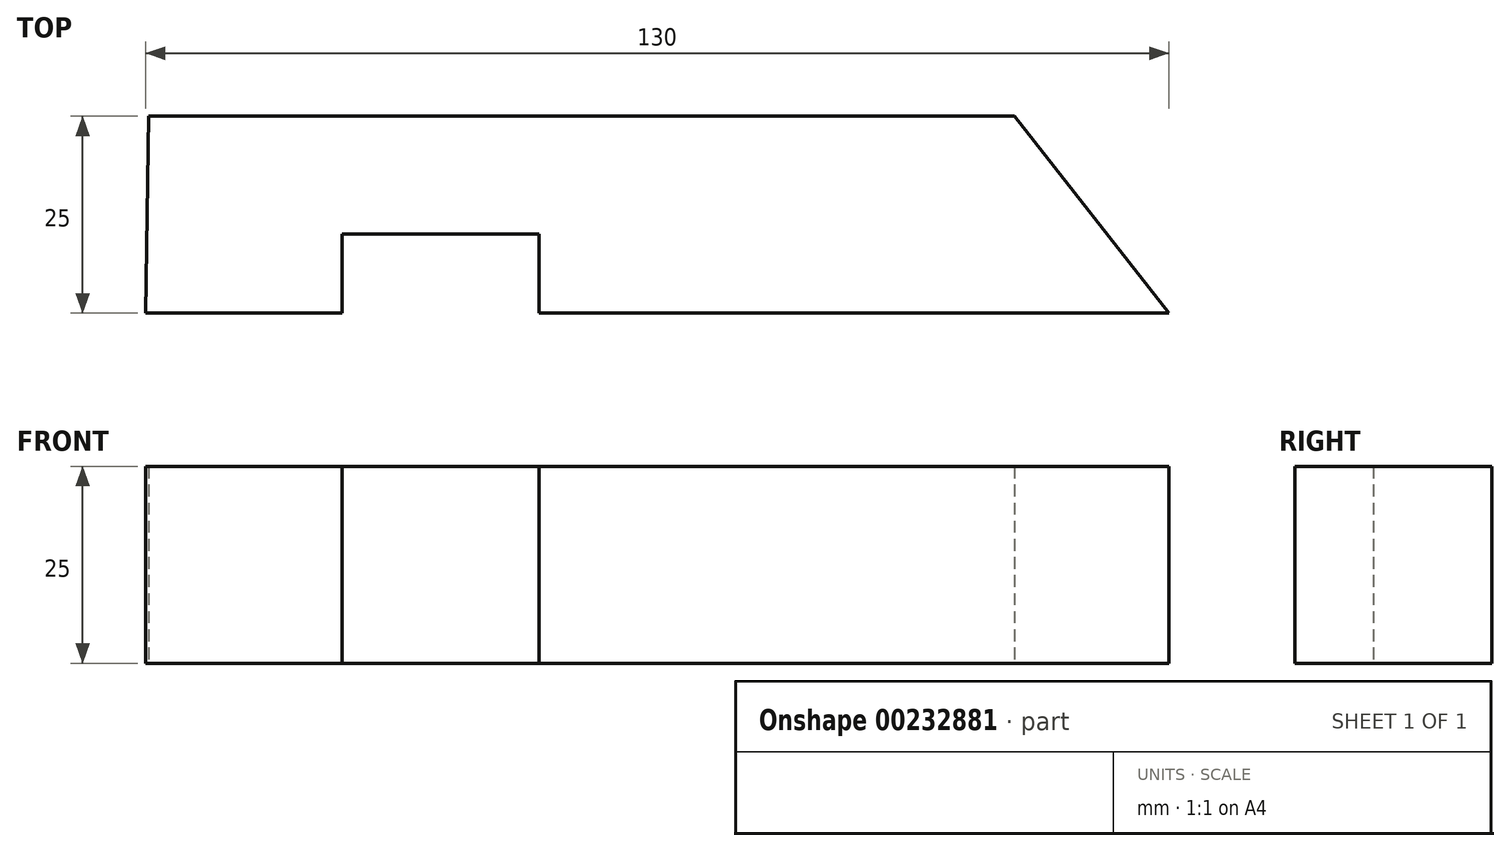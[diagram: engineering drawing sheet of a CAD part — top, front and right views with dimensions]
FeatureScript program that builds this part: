
annotation { "Feature Type Name" : "Feature", "Feature Type Description" : "" }
export const myFeature = defineFeature(function(context is Context, id is Id, definition is map)
    precondition{}
    {
        {
            var Q0;
            Q0=qCreatedBy(makeId("Top.planeOp"),FACE);
            var sketch = newSketch(context, id + "F0", { "sketchPlane" : qUnion([Q0])});
            skLineSegment(sketch, "E0", {"start": v(-52.89, 0.9) * mm, "end": v(57.11, 0.9) * mm});
            skLineSegment(sketch, "E1", {"start": v(57.11, 0.9) * mm, "end": v(76.74, -24.1) * mm});
            skLineSegment(sketch, "E2", {"start": v(76.74, -24.1) * mm, "end": v(-3.26, -24.1) * mm});
            skLineSegment(sketch, "E3", {"start": v(-3.26, -24.1) * mm, "end": v(-3.26, -14.1) * mm});
            skLineSegment(sketch, "E4", {"start": v(-3.26, -14.1) * mm, "end": v(-28.26, -14.1) * mm});
            skLineSegment(sketch, "E5", {"start": v(-28.26, -14.1) * mm, "end": v(-28.26, -24.1) * mm});
            skLineSegment(sketch, "E6", {"start": v(-28.26, -24.1) * mm, "end": v(-53.26, -24.1) * mm});
            skLineSegment(sketch, "E7", {"start": v(-53.26, -24.1) * mm, "end": v(-52.89, 0.9) * mm});
            skSolve(sketch);
        }
        {
            var Q0;
            Q0 = qSketchRegion(id + "F0", true);
            extrude(context, id + "F1", {"entities" : qUnion([Q0]), "depth" : 25 * mm});
        }
    });
